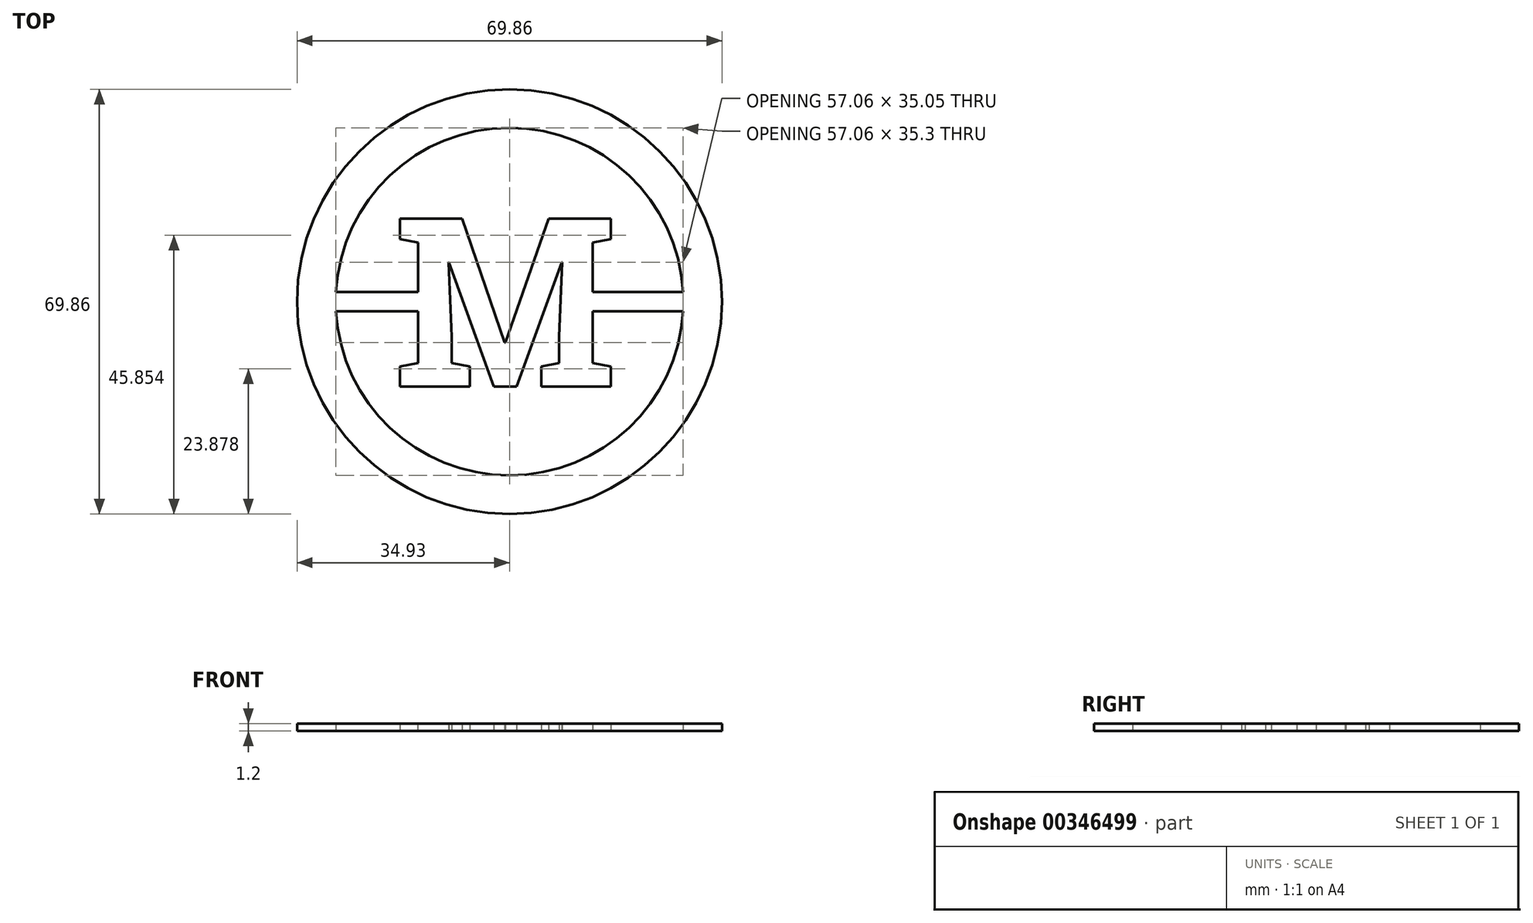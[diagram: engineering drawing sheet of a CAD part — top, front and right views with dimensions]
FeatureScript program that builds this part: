
annotation { "Feature Type Name" : "Feature", "Feature Type Description" : "" }
export const myFeature = defineFeature(function(context is Context, id is Id, definition is map)
    precondition{}
    {
        {
            var Q0;
            Q0=qCreatedBy(makeId("Top.planeOp"),FACE);
            var sketch = newSketch(context, id + "F0", { "sketchPlane" : qUnion([Q0])});
            skText(sketch, "E0", { "text": "M", "fontName": "RobotoSlab-Bold.ttf"});
            skLineSegment(sketch, "E1", {"start": v(0, 0) * mm, "end": v(19.05, 0) * mm, "construction": true});
            skCircle(sketch, "E2", {"center": v(0, 0) * mm, "radius": 34.93 * mm});
            skPoint(sketch, "E3.end.orphan", {"position": v(-28.53, 1.59) * mm});
            skPoint(sketch, "E3.start.orphan", {"position": v(-28.53, -1.59) * mm});
            skCircle(sketch, "E4", {"center": v(0, 0) * mm, "radius": 28.58 * mm});
            const initialGuessF0  = {"E0": [-0.01905, -0.014, 1, 0, 0.028]};
            skSetInitialGuess(sketch, initialGuessF0);
            skSolve(sketch);
        }
        {
            var Q0;
            Q0 = qSketchRegion(id + "F0", true);
            extrude(context, id + "F1", {"entities" : qUnion([Q0]), "depth" : .2 * 6 * mm});
        }
        {
            var Q0;
            Q0=qCreatedBy(makeId("Top.planeOp"),FACE);
            var sketch = newSketch(context, id + "F2", { "sketchPlane" : qUnion([Q0])});
            skText(sketch, "E5", { "text": "M", "fontName": "RobotoSlab-Bold.ttf"});
            skLineSegment(sketch, "E6", {"start": v(0, 0) * mm, "end": v(19.05, 0) * mm, "construction": true});
            const initialGuessF2  = {"E5": [-0.01905, -0.014, 1, 0, 0.028]};
            skSetInitialGuess(sketch, initialGuessF2);
            skSolve(sketch);
        }
        {
            var Q0;
            Q0 = qSketchRegion(id + "F2", true);
            var Q1;
            Q1=makeQuery(id+"F1.opExtrude","CAP_FACE",FACE,{"disambiguationData":[OSD([sQuery(id+"F0.wireOp",EDGE,"E2"),sQuery(id+"F0.wireOp",EDGE,"E4")])],"isStart":false});
            extrude(context, id + "F3", {"entities" : qUnion([Q0]), "endBound" : BoundingType.UP_TO_SURFACE, "endBoundEntityFace" : qUnion([Q1]), "depth" : 25.4 * mm});
        }
        {
            var Q0;
            Q0=qCreatedBy(makeId("Top.planeOp"),FACE);
            var sketch = newSketch(context, id + "F4", { "sketchPlane" : qUnion([Q0])});
            skArc(sketch, "E7.0", {"start": v(-28.53, 1.59) * mm, "mid": v(-28.57, 0) * mm, "end": v(-28.53, -1.59) * mm});
            skLineSegment(sketch, "E8.0", {"start": v(-15.05, -10.1) * mm, "end": v(-15.05, 9.73) * mm, "construction": true});
            skLineSegment(sketch, "E9", {"start": v(-28.53, 1.59) * mm, "end": v(-15.05, 1.59) * mm});
            skLineSegment(sketch, "E10", {"start": v(-15.05, 1.59) * mm, "end": v(-15.05, -1.59) * mm});
            skLineSegment(sketch, "E11", {"start": v(-15.05, -1.59) * mm, "end": v(-28.53, -1.59) * mm});
            skLineSegment(sketch, "E12", {"start": v(-15.05, 0) * mm, "end": v(-28.58, 0) * mm, "construction": true});
            skLineSegment(sketch, "E13", {"start": v(0, 0) * mm, "end": v(0, 25.4) * mm, "construction": true});
            skArc(sketch, "E14.MirrorCS", {"start": v(28.53, 1.59) * mm, "mid": v(28.58, 0) * mm, "end": v(28.53, -1.59) * mm});
            skLineSegment(sketch, "E15.0", {"start": v(13.7, 9.73) * mm, "end": v(13.7, -10.1) * mm, "construction": true});
            skLineSegment(sketch, "E16", {"start": v(28.53, 1.59) * mm, "end": v(13.7, 1.59) * mm});
            skLineSegment(sketch, "E17", {"start": v(28.53, -1.59) * mm, "end": v(13.7, -1.59) * mm});
            skLineSegment(sketch, "E18", {"start": v(13.7, -1.59) * mm, "end": v(13.7, 1.59) * mm});
            skSolve(sketch);
        }
        {
            var Q0;
            Q0 = qSketchRegion(id + "F4", true);
            var Q1;
            Q1=makeQuery(id+"F1.opExtrude","CAP_FACE",FACE,{"disambiguationData":[OSD([sQuery(id+"F0.wireOp",EDGE,"E2"),sQuery(id+"F0.wireOp",EDGE,"E4")])],"isStart":false});
            extrude(context, id + "F5", {"entities" : qUnion([Q0]), "operationType" : NewBodyOperationType.ADD, "endBound" : BoundingType.UP_TO_SURFACE, "endBoundEntityFace" : qUnion([Q1]), "depth" : 25.4 * mm});
        }
    });
